# Revit family: Electronics_Desono_Biamp_Two-Way-Surface-Mount-Loudspeaker_MASK6CT
name_source: partatom
category: Communication Devices
units: mm (PartAtom-declared; Revit-internal decimal feet)

## family parameters
Cut with Voids When Loaded = No
Host = Face
Maintain Annotation Orientation = No
OmniClass Number = 23.85.10.11.14.14.14
Part Type = Normal
Room Calculation Point = No
Round Connector Dimension = Use Diameter
Shared = No

## types (2) — shared parameters
Connector Description = Terminal strip; Low impedance 16 ohms, 70V/100V operation
Continuous Power Handling Nominal Impedance = 49V; 150W @ 16Ω (600W peak)
Controls = Power tap / low impedance selector switch
Default Elevation = 4' - 0"
Depth = 0' - 7 1/2"
Description = Desono™ MASK6CT Two-Way 6.5-Inch Surface Mount Loudspeaker
Environmental = IP64 per IEC 60529
Height = 1' - 1"
Input Connection = Audio connections made at the ClickMount bracket;lever-action input and output terminals accept up to 16 AWG conductors
Manufacturer = Biamp
Mounting Provisions = ClickMount bracket
Nominal Beamwidth  (H x V) = 100 x 50
Nominal Maximum SPL @ 1m = Peak - 118dB; Continuous - 112dB
Nominal Sensitivity @ 1m = 1W - 90dB; 2.83V - 87dB
Operating Environment = Indoor/Outdoor
Operating Mode = Passive
Operating Range (-10dB) = 65 Hz to 22 kHz
Product Documentation Link = https://downloads.biamp.com
Product Page URL = https://www.biamp.com
Product data url = https://www.bimobject.com
Protection = 3-step self-resetting protection
Recommended Amplifers = 150W-300W @ 16Ω (49V - 69V)
Transducers = LF 1 x 6.5 (165 mm) coated paper cone HF 1 x 1 (25 mm) soft dome
Transformer = 70V: 60W, 30W, 15W, 7.5W, 3W; 100V: 60W, 30W, 15W, 6W
URL = https://www.biamp.com
Weight = 9.70 lb
Width = 0' - 8"

## per-type parameters (varying)
| type | Bracket Material | Grill Material | Housing Material |
| MASK6CT W | Biamp - Plastic - White | Biamp - Plastic - White(Grid) | Biamp - Plastic - White |
| MASK6CT B | Biamp - Plastic - Black | Biamp - Plastic - Black(Grid) | Biamp - Plastic - Black |

note: column(s) folded — value = type name in every type: Model

## geometry (parser evidence)
native form markers: Sweep x15
no freeform markers — native parametric forms only
